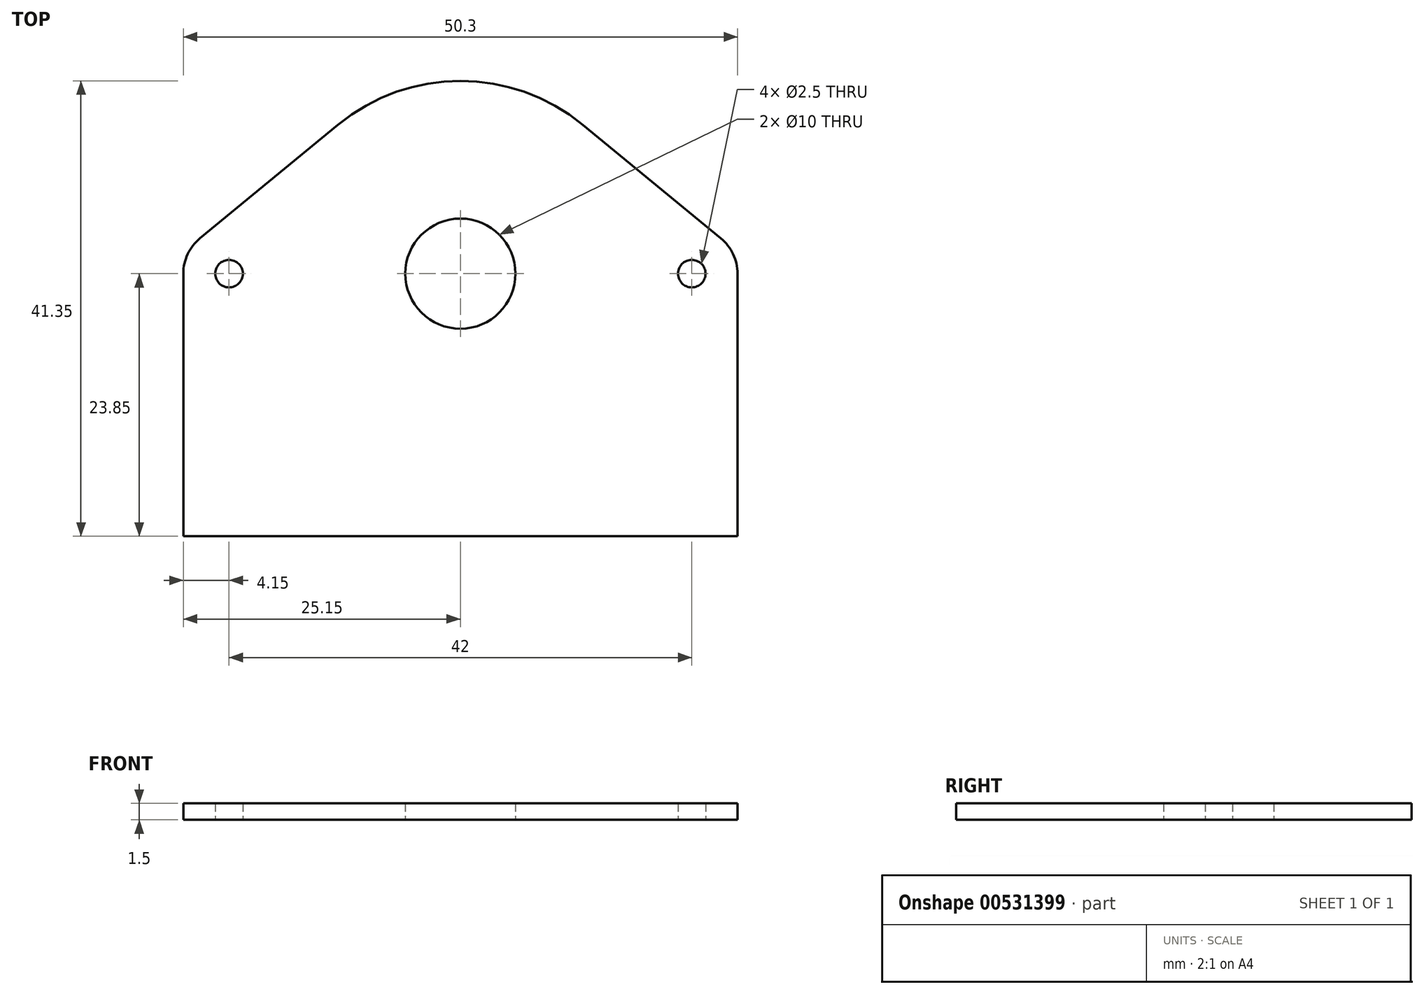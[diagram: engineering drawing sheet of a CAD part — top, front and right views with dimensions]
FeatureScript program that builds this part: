
annotation { "Feature Type Name" : "Feature", "Feature Type Description" : "" }
export const myFeature = defineFeature(function(context is Context, id is Id, definition is map)
    precondition{}
    {
        {
            var Q0;
            Q0=qCreatedBy(makeId("Top.planeOp"),FACE);
            var sketch = newSketch(context, id + "F0", { "sketchPlane" : qUnion([Q0])});
            skPoint(sketch, "E0.middle", {"position": v(0, 0) * mm});
            skCircle(sketch, "E1", {"center": v(0, 0) * mm, "radius": 5 * mm});
            skPoint(sketch, "E2", {"position": v(-19.75, 0) * mm});
            skPoint(sketch, "E3.MirrorP", {"position": v(19.75, 0) * mm});
            skCircle(sketch, "E4", {"center": v(21, 0) * mm, "radius": 1.25 * mm});
            skCircle(sketch, "E5.MirrorC", {"center": v(-21, 0) * mm, "radius": 1.25 * mm});
            skArc(sketch, "E6", {"start": v(11.2, 13.44) * mm, "mid": v(0, 17.5) * mm, "end": v(-11.2, 13.44) * mm});
            skPoint(sketch, "E0.right.start.orphan", {"position": v(38.1, -38.1) * mm});
            skPoint(sketch, "E0.top.end.orphan", {"position": v(38.1, 38.1) * mm});
            skPoint(sketch, "E0.left.end.orphan", {"position": v(-38.1, 38.1) * mm});
            skPoint(sketch, "E0.left.start.orphan", {"position": v(-38.1, -38.1) * mm});
            skPoint(sketch, "E7.MirrorCS.end.orphan", {"position": v(25.06, -20.14) * mm});
            skPoint(sketch, "E7.MirrorCS.start.orphan", {"position": v(25.15, 0) * mm});
            skPoint(sketch, "E8.MirrorCS.start.orphan", {"position": v(23.6, 3.12) * mm});
            skPoint(sketch, "E9.MirrorCS.start.orphan", {"position": v(11.2, 13.44) * mm});
            skPoint(sketch, "E10.end.orphan", {"position": v(-25.06, -20.14) * mm});
            skPoint(sketch, "E11.trimOffspring.end.orphan", {"position": v(-25.15, 0) * mm});
            skPoint(sketch, "E12.end.orphan", {"position": v(-23.6, 3.12) * mm});
            skPoint(sketch, "E12.start.orphan", {"position": v(-11.2, 13.44) * mm});
            skArc(sketch, "E13", {"start": v(25.15, 0) * mm, "mid": v(24.75, 1.77) * mm, "end": v(23.64, 3.2) * mm});
            skLineSegment(sketch, "E14", {"start": v(11.13, 13.5) * mm, "end": v(23.64, 3.2) * mm});
            skLineSegment(sketch, "E15", {"start": v(25.15, 0) * mm, "end": v(25.15, -15.7) * mm});
            skLineSegment(sketch, "E16.MirrorCS", {"start": v(-25.15, 0) * mm, "end": v(-25.15, -15.7) * mm});
            skLineSegment(sketch, "E17.MirrorCS", {"start": v(-11.13, 13.5) * mm, "end": v(-23.64, 3.2) * mm});
            skArc(sketch, "E18.MirrorCS", {"start": v(-25.15, 0) * mm, "mid": v(-24.75, 1.77) * mm, "end": v(-23.64, 3.2) * mm});
            skPoint(sketch, "E19", {"position": v(0, -23.85) * mm});
            skLineSegment(sketch, "E20", {"start": v(0, -23.85) * mm, "end": v(-25.15, -23.85) * mm});
            skLineSegment(sketch, "E21", {"start": v(0, -23.85) * mm, "end": v(25.15, -23.85) * mm});
            skLineSegment(sketch, "E22", {"start": v(-25.15, -15.7) * mm, "end": v(-25.15, -23.85) * mm});
            skLineSegment(sketch, "E23", {"start": v(25.15, -15.7) * mm, "end": v(25.15, -23.85) * mm});
            skPoint(sketch, "E24.orphan", {"position": v(29.6, -23.85) * mm});
            skSolve(sketch);
        }
        {
            var Q0;
            Q0=makeQuery(id+"F0.imprint","IMPRINT",FACE,{"disambiguationData":[TD([[makeQuery(id+"F0.imprint","IMPRINT",EDGE,{"derivedFrom":sQuery(id+"F0.wireOp",EDGE,"E1")}),-1.0]])]});
            extrude(context, id + "F1", {"entities" : qUnion([Q0]), "endBound" : BoundingType.SYMMETRIC, "depth" : 1.5 * mm, "offsetDistance" : 25.4 * mm});
        }
    });
